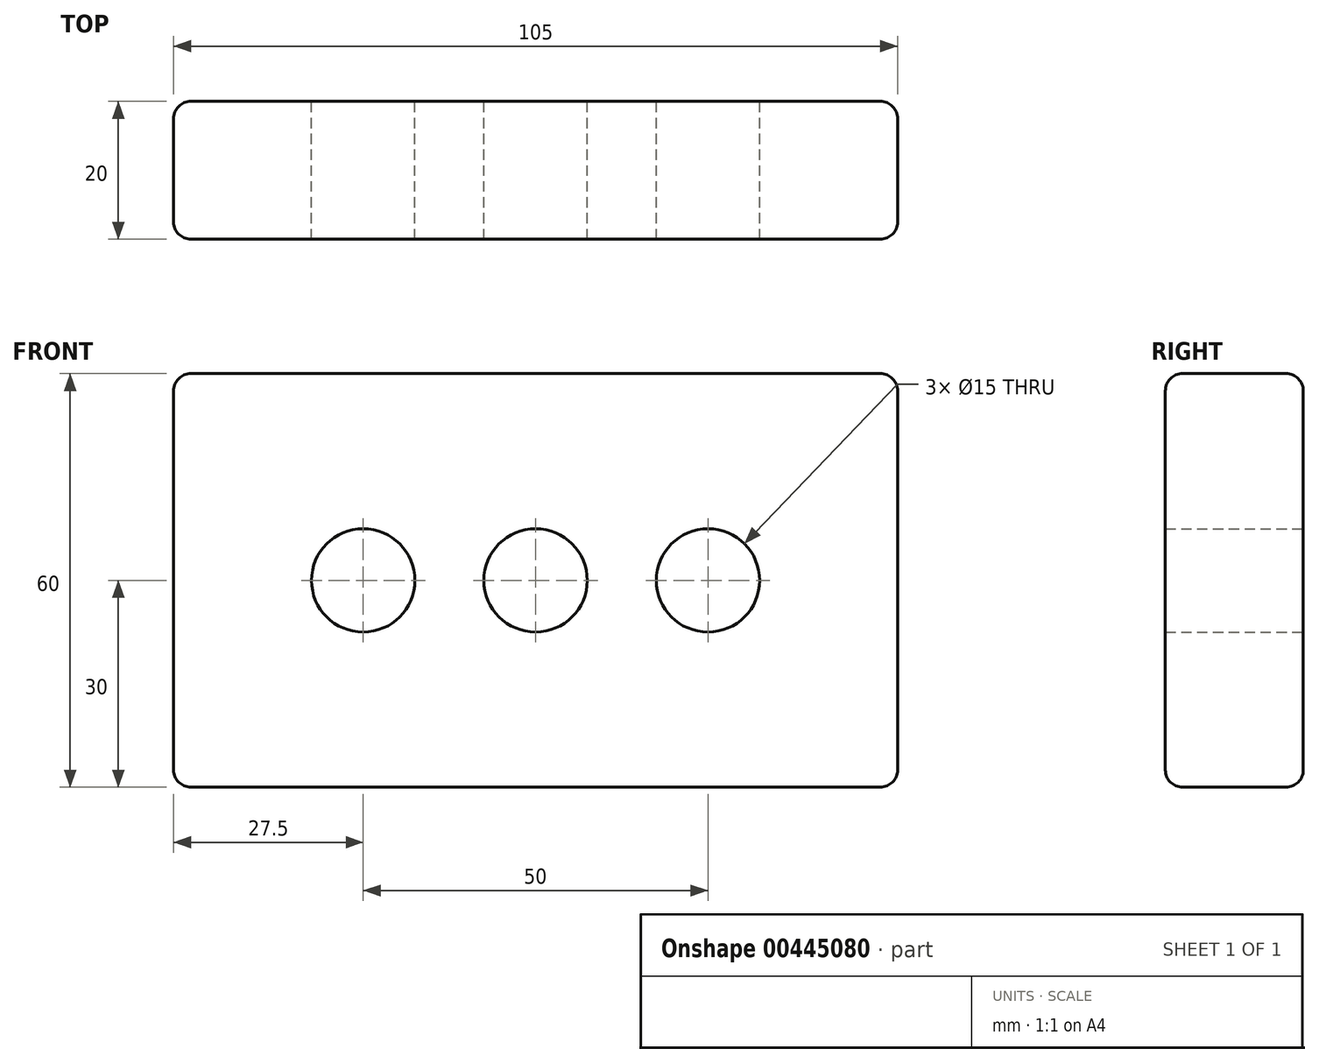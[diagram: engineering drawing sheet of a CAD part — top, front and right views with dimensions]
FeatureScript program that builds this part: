
annotation { "Feature Type Name" : "Feature", "Feature Type Description" : "" }
export const myFeature = defineFeature(function(context is Context, id is Id, definition is map)
    precondition{}
    {
        {
            var Q0;
            Q0=qCreatedBy(makeId("Front.planeOp"),FACE);
            var sketch = newSketch(context, id + "F0", { "sketchPlane" : qUnion([Q0])});
            skLineSegment(sketch, "E0.bottom", {"start": v(-52.5, 30) * mm, "end": v(52.5, 30) * mm});
            skLineSegment(sketch, "E0.top", {"start": v(-52.5, -30) * mm, "end": v(52.5, -30) * mm});
            skLineSegment(sketch, "E0.left", {"start": v(-52.5, 30) * mm, "end": v(-52.5, -30) * mm});
            skLineSegment(sketch, "E0.right", {"start": v(52.5, 30) * mm, "end": v(52.5, -30) * mm});
            skPoint(sketch, "E0.middle", {"position": v(0, 0) * mm});
            skCircle(sketch, "E1", {"center": v(0, 0) * mm, "radius": 7.5 * mm});
            skCircle(sketch, "E2", {"center": v(-25, 0) * mm, "radius": 7.5 * mm});
            skCircle(sketch, "E3", {"center": v(25, 0) * mm, "radius": 7.5 * mm});
            skSolve(sketch);
        }
        {
            var Q0;
            Q0=makeQuery(id+"F0.imprint","IMPRINT",FACE,{"disambiguationData":[TD([[makeQuery(id+"F0.imprint","IMPRINT",EDGE,{"derivedFrom":sQuery(id+"F0.wireOp",EDGE,"E0.bottom")}),-1.0]])]});
            extrude(context, id + "F1", {"entities" : qUnion([Q0]), "depth" : 20 * mm});
        }
        {
            var Q0;
            Q0=makeQuery(id+"F1.opExtrude","CAP_EDGE",EDGE,{"disambiguationData":[OSD([sQuery(id+"F0.wireOp",EDGE,"E0.bottom")])],"isStart":false});
            var Q1;
            Q1=makeQuery(id+"F1.opExtrude","SWEPT_EDGE",EDGE,{"disambiguationData":[OSD([sQuery(id+"F0.wireOp",EDGE,"E0.bottom"),sQuery(id+"F0.wireOp",EDGE,"E0.left")])]});
            var Q2;
            Q2=makeQuery(id+"F1.opExtrude","CAP_EDGE",EDGE,{"disambiguationData":[OSD([sQuery(id+"F0.wireOp",EDGE,"E0.bottom")])],"isStart":true});
            var Q3;
            Q3=makeQuery(id+"F1.opExtrude","SWEPT_EDGE",EDGE,{"disambiguationData":[OSD([sQuery(id+"F0.wireOp",EDGE,"E0.bottom"),sQuery(id+"F0.wireOp",EDGE,"E0.right")])]});
            var Q4;
            Q4=makeQuery(id+"F1.opExtrude","CAP_EDGE",EDGE,{"disambiguationData":[OSD([sQuery(id+"F0.wireOp",EDGE,"E0.right")])],"isStart":false});
            var Q5;
            Q5=makeQuery(id+"F1.opExtrude","CAP_EDGE",EDGE,{"disambiguationData":[OSD([sQuery(id+"F0.wireOp",EDGE,"E0.right")])],"isStart":true});
            var Q6;
            Q6=makeQuery(id+"F1.opExtrude","SWEPT_EDGE",EDGE,{"disambiguationData":[OSD([sQuery(id+"F0.wireOp",EDGE,"E0.top"),sQuery(id+"F0.wireOp",EDGE,"E0.right")])]});
            var Q7;
            Q7=makeQuery(id+"F1.opExtrude","CAP_EDGE",EDGE,{"disambiguationData":[OSD([sQuery(id+"F0.wireOp",EDGE,"E0.top")])],"isStart":false});
            var Q8;
            Q8=makeQuery(id+"F1.opExtrude","CAP_EDGE",EDGE,{"disambiguationData":[OSD([sQuery(id+"F0.wireOp",EDGE,"E0.left")])],"isStart":true});
            var Q9;
            Q9=makeQuery(id+"F1.opExtrude","SWEPT_EDGE",EDGE,{"disambiguationData":[OSD([sQuery(id+"F0.wireOp",EDGE,"E0.top"),sQuery(id+"F0.wireOp",EDGE,"E0.left")])]});
            var Q10;
            Q10=makeQuery(id+"F1.opExtrude","CAP_EDGE",EDGE,{"disambiguationData":[OSD([sQuery(id+"F0.wireOp",EDGE,"E0.top")])],"isStart":true});
            var Q11;
            Q11=makeQuery(id+"F1.opExtrude","CAP_EDGE",EDGE,{"disambiguationData":[OSD([sQuery(id+"F0.wireOp",EDGE,"E0.left")])],"isStart":false});
            fillet(context, id + "F2", {"entities" : qUnion([Q0, Q1, Q2, Q3, Q4, Q5, Q6, Q7, Q8, Q9, Q10, Q11]), "radius" : 2.5 * mm, "tangentPropagation" : true, "allowEdgeOverflow" : false});
        }
    });
